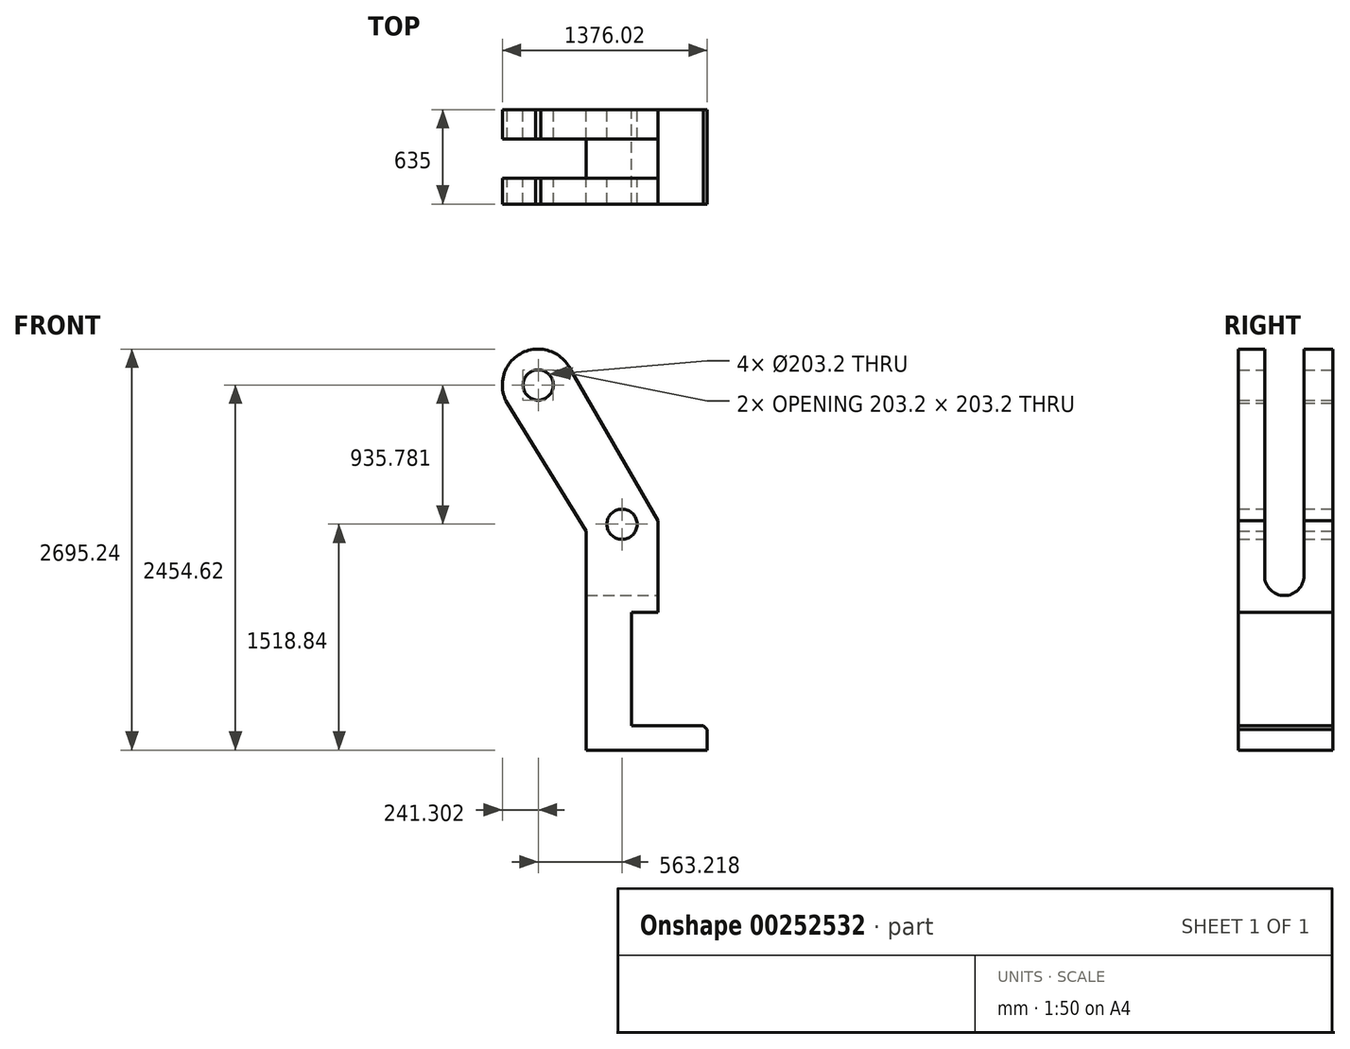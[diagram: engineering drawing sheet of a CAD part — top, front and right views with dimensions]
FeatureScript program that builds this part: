
annotation { "Feature Type Name" : "Feature", "Feature Type Description" : "" }
export const myFeature = defineFeature(function(context is Context, id is Id, definition is map)
    precondition{}
    {
        {
            var Q0;
            Q0=qCreatedBy(makeId("Front.planeOp"),FACE);
            var sketch = newSketch(context, id + "F0", { "sketchPlane" : qUnion([Q0])});
            skLineSegment(sketch, "E0.bottom", {"start": v(0, 0) * mm, "end": v(-812.8, 0) * mm});
            skLineSegment(sketch, "E0.top", {"start": v(0, 165.1) * mm, "end": v(-508, 165.1) * mm});
            skLineSegment(sketch, "E0.left", {"start": v(0, 0) * mm, "end": v(0, 165.1) * mm});
            skLineSegment(sketch, "E0.right", {"start": v(-812.8, 0) * mm, "end": v(-812.8, 165.1) * mm});
            skLineSegment(sketch, "E1.left", {"start": v(-812.8, 165.1) * mm, "end": v(-812.8, 1473.2) * mm});
            skLineSegment(sketch, "E1.right", {"start": v(-330.2, 927.1) * mm, "end": v(-330.2, 1473.2) * mm});
            skLineSegment(sketch, "E2.bottom", {"start": v(-330.2, 927.1) * mm, "end": v(-508, 927.1) * mm});
            skLineSegment(sketch, "E2.right", {"start": v(-508, 927.1) * mm, "end": v(-508, 165.1) * mm});
            skLineSegment(sketch, "E3", {"start": v(-812.8, 1473.2) * mm, "end": v(-1343.7, 2333.97) * mm});
            skLineSegment(sketch, "E4", {"start": v(-925.75, 2575.27) * mm, "end": v(-330.2, 1543.75) * mm});
            skLineSegment(sketch, "E5", {"start": v(-330.2, 1473.2) * mm, "end": v(-330.2, 1543.75) * mm});
            skArc(sketch, "E6", {"start": v(-925.75, 2575.27) * mm, "mid": v(-1255.37, 2663.6) * mm, "end": v(-1343.7, 2333.97) * mm});
            skCircle(sketch, "E7", {"center": v(-1134.72, 2454.62) * mm, "radius": 101.6 * mm});
            skCircle(sketch, "E8", {"center": v(-571.5, 1518.84) * mm, "radius": 101.6 * mm});
            skPoint(sketch, "E9", {"position": v(-1255.37, 2663.6) * mm});
            skLineSegment(sketch, "E10", {"start": v(-1116.56, 2695.24) * mm, "end": v(-1152.88, 2695.24) * mm});
            skPoint(sketch, "E11", {"position": v(-1116.56, 2695.24) * mm});
            skSolve(sketch);
        }
        {
            var Q0;
            Q0=makeQuery(id+"F0.imprint","IMPRINT",FACE,{"disambiguationData":[TD([[makeQuery(id+"F0.imprint","IMPRINT",EDGE,{"derivedFrom":sQuery(id+"F0.wireOp",EDGE,"E0.bottom")}),-1.0]])]});
            extrude(context, id + "F1", {"entities" : qUnion([Q0]), "depth" : 635 * mm});
        }
        {
            var Q0;
            Q0=makeQuery(id+"F1.opExtrude","SWEPT_FACE",FACE,{"disambiguationData":[OSD([sQuery(id+"F0.wireOp",EDGE,"E1.right"),sQuery(id+"F0.wireOp",EDGE,"E5")])]});
            var sketch = newSketch(context, id + "F2", { "sketchPlane" : qUnion([Q0])});
            skLineSegment(sketch, "E12.bottom", {"start": v(-460.14, 1543.75) * mm, "end": v(-195.98, 1543.75) * mm});
            skLineSegment(sketch, "E12.top", {"start": v(-460.14, 1171.24) * mm, "end": v(-195.98, 1171.24) * mm});
            skLineSegment(sketch, "E12.left", {"start": v(-460.14, 1543.75) * mm, "end": v(-460.14, 1171.24) * mm});
            skLineSegment(sketch, "E12.right", {"start": v(-195.98, 1543.75) * mm, "end": v(-195.98, 1171.24) * mm});
            skArc(sketch, "E13", {"start": v(-460.14, 1171.24) * mm, "mid": v(-328.06, 1039.16) * mm, "end": v(-195.98, 1171.24) * mm});
            skPoint(sketch, "E14", {"position": v(-328.06, 1543.75) * mm});
            skLineSegment(sketch, "E15.top", {"start": v(-460.14, 2695.24) * mm, "end": v(-195.98, 2695.24) * mm});
            skLineSegment(sketch, "E15.left", {"start": v(-460.14, 1543.75) * mm, "end": v(-460.14, 2695.24) * mm});
            skLineSegment(sketch, "E15.right", {"start": v(-195.98, 1543.75) * mm, "end": v(-195.98, 2695.24) * mm});
            skPoint(sketch, "E16", {"position": v(-328.06, 1039.16) * mm});
            skSolve(sketch);
        }
        {
            var Q0;
            Q0=makeQuery(id+"F2.imprint","IMPRINT",FACE,{"disambiguationData":[TD([[makeQuery(id+"F2.imprint","IMPRINT",EDGE,{"derivedFrom":sQuery(id+"F2.wireOp",EDGE,"E12.bottom")}),1.0]])]});
            var Q1;
            Q1=makeQuery(id+"F2.imprint","IMPRINT",FACE,{"disambiguationData":[TD([[makeQuery(id+"F2.imprint","IMPRINT",EDGE,{"derivedFrom":sQuery(id+"F2.wireOp",EDGE,"E12.top")}),1.0]])]});
            var Q2;
            Q2=makeQuery(id+"F2.imprint","IMPRINT",FACE,{"disambiguationData":[TD([[makeQuery(id+"F2.imprint","IMPRINT",EDGE,{"derivedFrom":sQuery(id+"F2.wireOp",EDGE,"E12.top")}),-1.0]])]});
            extrude(context, id + "F3", {"entities" : qUnion([Q0, Q1, Q2]), "operationType" : NewBodyOperationType.REMOVE, "endBound" : BoundingType.THROUGH_ALL, "oppositeDirection" : true, "depth" : 25.4 * mm});
        }
        {
            var Q0;
            Q0=makeQuery(id+"F1.opExtrude","SWEPT_EDGE",EDGE,{"disambiguationData":[OSD([sQuery(id+"F0.wireOp",EDGE,"E0.top"),sQuery(id+"F0.wireOp",EDGE,"E0.left")])]});
            chamfer(context, id + "F4", {"entities" : qUnion([Q0]), "chamferType" : ChamferType.OFFSET_ANGLE, "width" : 25.4 * mm, "oppositeDirection" : false, "angle" : 45 * degree, "tangentPropagation" : true});
        }
    });
